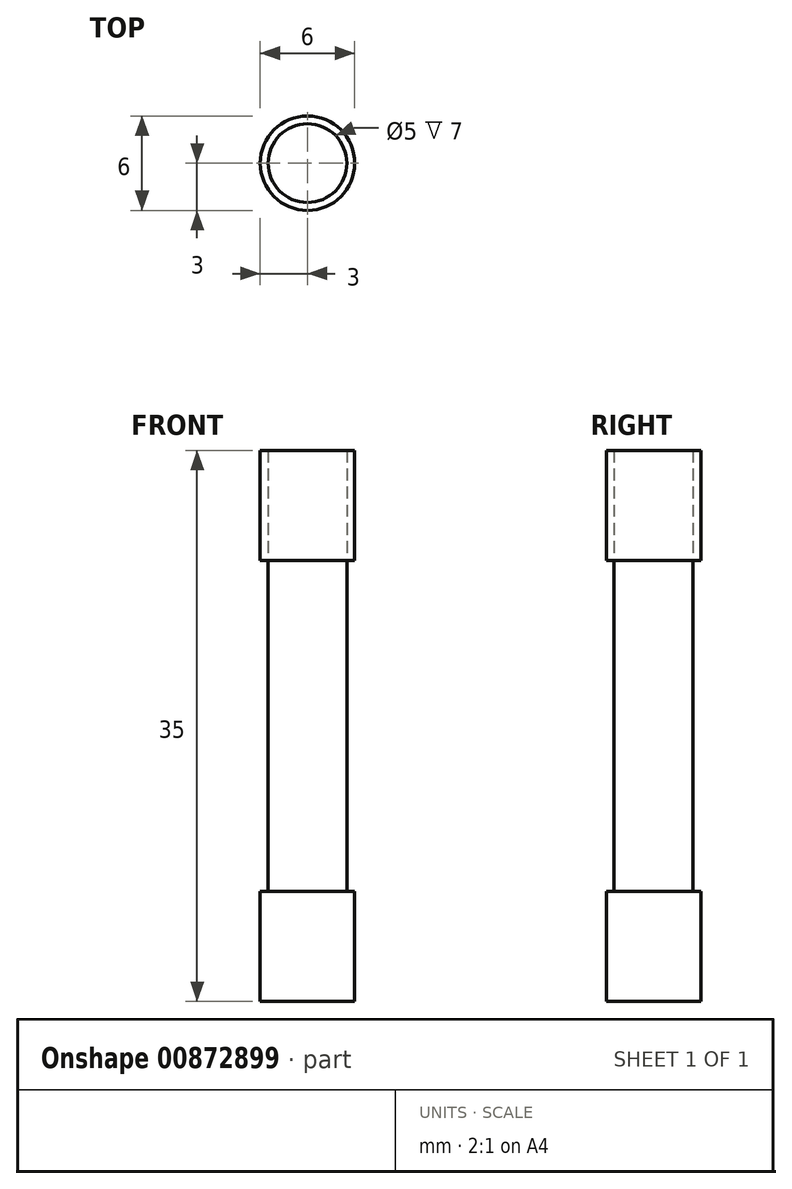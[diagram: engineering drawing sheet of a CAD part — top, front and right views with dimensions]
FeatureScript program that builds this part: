
annotation { "Feature Type Name" : "Feature", "Feature Type Description" : "" }
export const myFeature = defineFeature(function(context is Context, id is Id, definition is map)
    precondition{}
    {
        {
            var Q0;
            Q0=qCreatedBy(makeId("Top.planeOp"),FACE);
            var sketch = newSketch(context, id + "F0", { "sketchPlane" : qUnion([Q0])});
            skCircle(sketch, "E0", {"center": v(0, 0) * mm, "radius": 3 * mm});
            skCircle(sketch, "E1", {"center": v(0, 0) * mm, "radius": 2.5 * mm});
            skSolve(sketch);
        }
        {
            var Q0;
            Q0=makeQuery(id+"F0.imprint","IMPRINT",FACE,{"disambiguationData":[TD([[makeQuery(id+"F0.imprint","IMPRINT",EDGE,{"derivedFrom":sQuery(id+"F0.wireOp",EDGE,"E0")}),1.0]])]});
            extrude(context, id + "F1", {"entities" : qUnion([Q0]), "depth" : 7 * mm, "offsetDistance" : 25 * mm});
        }
        {
            var Q0;
            Q0=makeQuery(id+"F0.imprint","IMPRINT",FACE,{"disambiguationData":[TD([[makeQuery(id+"F0.imprint","IMPRINT",EDGE,{"derivedFrom":sQuery(id+"F0.wireOp",EDGE,"E1")}),1.0]])]});
            extrude(context, id + "F2", {"entities" : qUnion([Q0]), "operationType" : NewBodyOperationType.ADD, "depth" : 35 * mm, "offsetDistance" : 25 * mm});
        }
        {
            var Q0;
            Q0=makeQuery(id+"F0.imprint","IMPRINT",FACE,{"disambiguationData":[TD([[makeQuery(id+"F0.imprint","IMPRINT",EDGE,{"derivedFrom":sQuery(id+"F0.wireOp",EDGE,"E0")}),1.0]])]});
            extrude(context, id + "F3", {"entities" : qUnion([Q0]), "depth" : 7 * mm, "offsetDistance" : 25 * mm});
        }
        {
            var Q0;
            Q0=makeQuery(id+"F3.opExtrude","SWEPT_BODY",BODY,{"disambiguationData":[OSD([sQuery(id+"F0.wireOp",EDGE,"E0"),sQuery(id+"F0.wireOp",EDGE,"E1")])]});
            transform(context, id + "F4", {"entities" : qUnion([Q0]), "transformType" : TransformType.TRANSLATION_3D, "dx" : 0 * mm, "dy" : 0 * mm, "dz" : 28 * mm, "makeCopy" : false});
        }
    });
